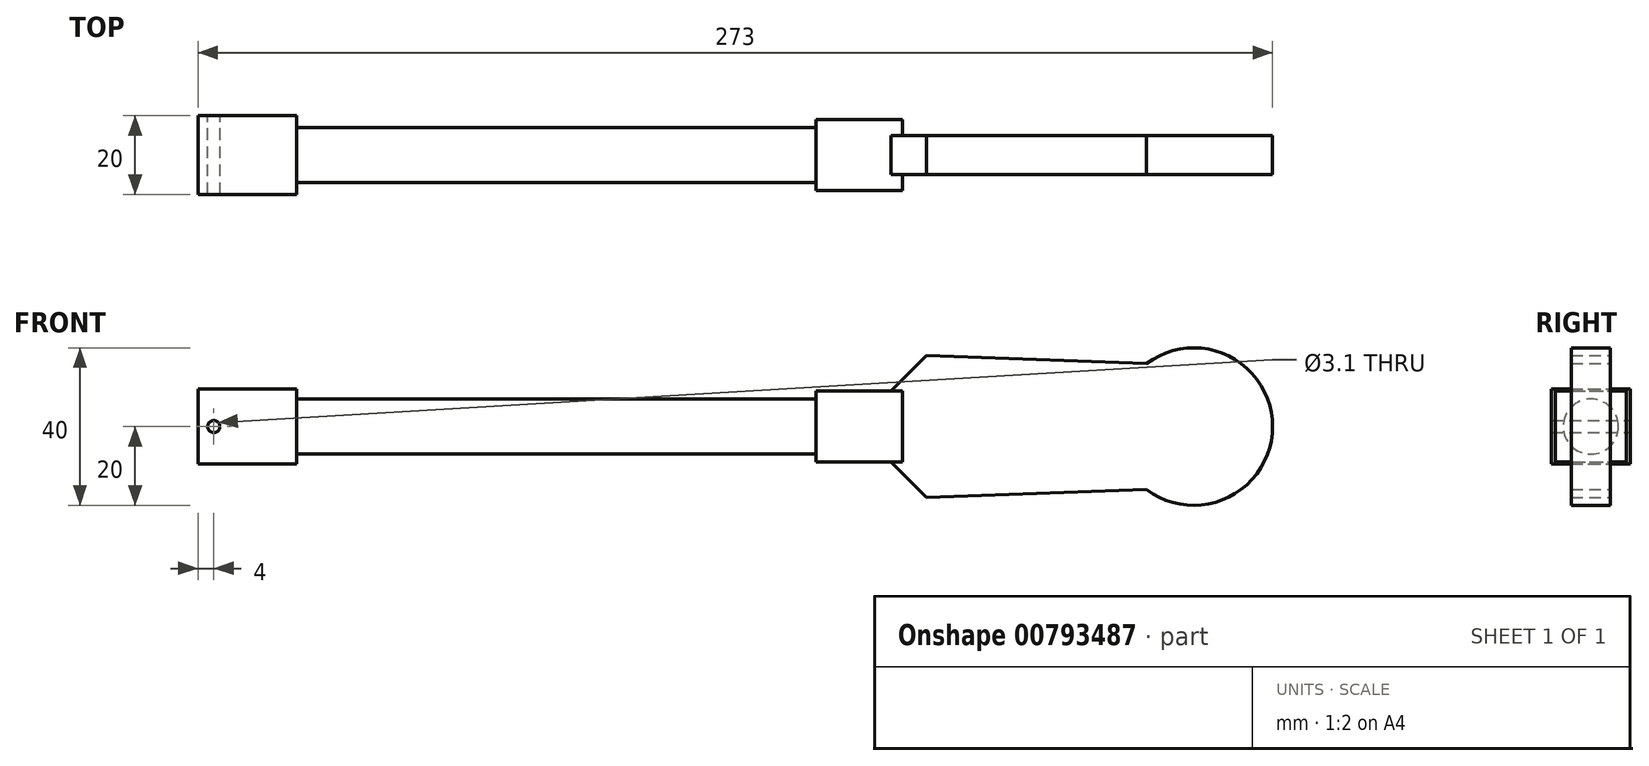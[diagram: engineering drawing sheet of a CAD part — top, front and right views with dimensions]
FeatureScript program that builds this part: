
annotation { "Feature Type Name" : "Feature", "Feature Type Description" : "" }
export const myFeature = defineFeature(function(context is Context, id is Id, definition is map)
    precondition{}
    {
        {
            var Q0;
            Q0=qCreatedBy(makeId("Front.planeOp"),FACE);
            var sketch = newSketch(context, id + "F0", { "sketchPlane" : qUnion([Q0])});
            skLineSegment(sketch, "E0", {"start": v(0, 0) * mm, "end": v(132, 0) * mm});
            skLineSegment(sketch, "E1", {"start": v(132, 0) * mm, "end": v(132, -7) * mm});
            skLineSegment(sketch, "E2", {"start": v(132, -7) * mm, "end": v(0, -7) * mm});
            skLineSegment(sketch, "E3", {"start": v(151, 9) * mm, "end": v(160, 18) * mm});
            skLineSegment(sketch, "E4", {"start": v(160, 18) * mm, "end": v(216, 16) * mm});
            skArc(sketch, "E5", {"start": v(216, -16) * mm, "mid": v(248, 0) * mm, "end": v(216, 16) * mm});
            skLineSegment(sketch, "E6", {"start": v(132, 0) * mm, "end": v(228, 0) * mm, "construction": true});
            skLineSegment(sketch, "E7.MirrorCS", {"start": v(160, -18) * mm, "end": v(216, -16) * mm});
            skLineSegment(sketch, "E8.MirrorCS", {"start": v(132, -9) * mm, "end": v(151, -9) * mm});
            skLineSegment(sketch, "E9.MirrorCS", {"start": v(151, -9) * mm, "end": v(160, -18) * mm});
            skLineSegment(sketch, "E10", {"start": v(154, -9) * mm, "end": v(151, -9) * mm});
            skLineSegment(sketch, "E11", {"start": v(151, 9) * mm, "end": v(154, 9) * mm});
            skLineSegment(sketch, "E12", {"start": v(154, -9) * mm, "end": v(154, 9) * mm});
            skLineSegment(sketch, "E13", {"start": v(0, 0) * mm, "end": v(0, -7) * mm});
            skLineSegment(sketch, "E14", {"start": v(132, -9) * mm, "end": v(132, -7) * mm});
            skLineSegment(sketch, "E15", {"start": v(132, 0) * mm, "end": v(132, 9) * mm});
            skLineSegment(sketch, "E16", {"start": v(151, 9) * mm, "end": v(132, 9) * mm});
            skPoint(sketch, "E17.center", {"position": v(0, 0) * mm});
            skLineSegment(sketch, "E18.bottom", {"start": v(0, 0) * mm, "end": v(-25, 0) * mm, "construction": true});
            skLineSegment(sketch, "E18.top", {"start": v(0, -9.5) * mm, "end": v(-25, -9.5) * mm});
            skLineSegment(sketch, "E18.left", {"start": v(0, 0) * mm, "end": v(0, -9.5) * mm});
            skLineSegment(sketch, "E19.MirrorCS", {"start": v(0, 9.5) * mm, "end": v(-25, 9.5) * mm});
            skLineSegment(sketch, "E20", {"start": v(-25, 9.5) * mm, "end": v(-25, -9.5) * mm});
            skLineSegment(sketch, "E21", {"start": v(0, 9.5) * mm, "end": v(0, 0) * mm});
            skCircle(sketch, "E22", {"center": v(-21, 0) * mm, "radius": 1.55 * mm});
            skSolve(sketch);
        }
        {
            var Q0;
            Q0=makeQuery(id+"F0.imprint","IMPRINT",FACE,{"disambiguationData":[TD([[makeQuery(id+"F0.imprint","IMPRINT",EDGE,{"derivedFrom":sQuery(id+"F0.wireOp",EDGE,"E0")}),-1.0]])]});
            var Q1;
            Q1=sQuery(id+"F0.wireOp",EDGE,"E0");
            revolve(context, id + "F1", {"surfaceOperationType" : NewSurfaceOperationType.NEW, "entities" : qUnion([Q0]), "axis" : qUnion([Q1]), "revolveType" : RevolveType.FULL});
        }
        {
            var Q0;
            Q0=makeQuery(id+"F0.imprint","IMPRINT",FACE,{"disambiguationData":[TD([[makeQuery(id+"F0.imprint","IMPRINT",EDGE,{"derivedFrom":sQuery(id+"F0.wireOp",EDGE,"E1")}),1.0]])]});
            extrude(context, id + "F2", {"entities" : qUnion([Q0]), "operationType" : NewBodyOperationType.ADD, "endBound" : BoundingType.SYMMETRIC, "depth" : 18 * mm, "offsetDistance" : 25 * mm});
        }
        {
            var Q0;
            Q0=makeQuery(id+"F0.imprint","IMPRINT",FACE,{"disambiguationData":[TD([[makeQuery(id+"F0.imprint","IMPRINT",EDGE,{"derivedFrom":sQuery(id+"F0.wireOp",EDGE,"E3")}),-1.0]])]});
            extrude(context, id + "F3", {"entities" : qUnion([Q0]), "operationType" : NewBodyOperationType.ADD, "endBound" : BoundingType.SYMMETRIC, "depth" : 10 * mm, "offsetDistance" : 25 * mm});
        }
        {
            var Q0;
            {var subQ2=sQuery(id+"F0.wireOp",EDGE,"E18.top");Q0=makeQuery(id+"F0.imprint","IMPRINT",FACE,{"disambiguationData":[TD([[makeQuery(id+"F0.imprint","IMPRINT",EDGE,{"derivedFrom":subQ2}),-1.0]])]});}
            extrude(context, id + "F4", {"entities" : qUnion([Q0]), "operationType" : NewBodyOperationType.ADD, "endBound" : BoundingType.SYMMETRIC, "depth" : 20 * mm, "offsetDistance" : 25 * mm});
        }
    });
